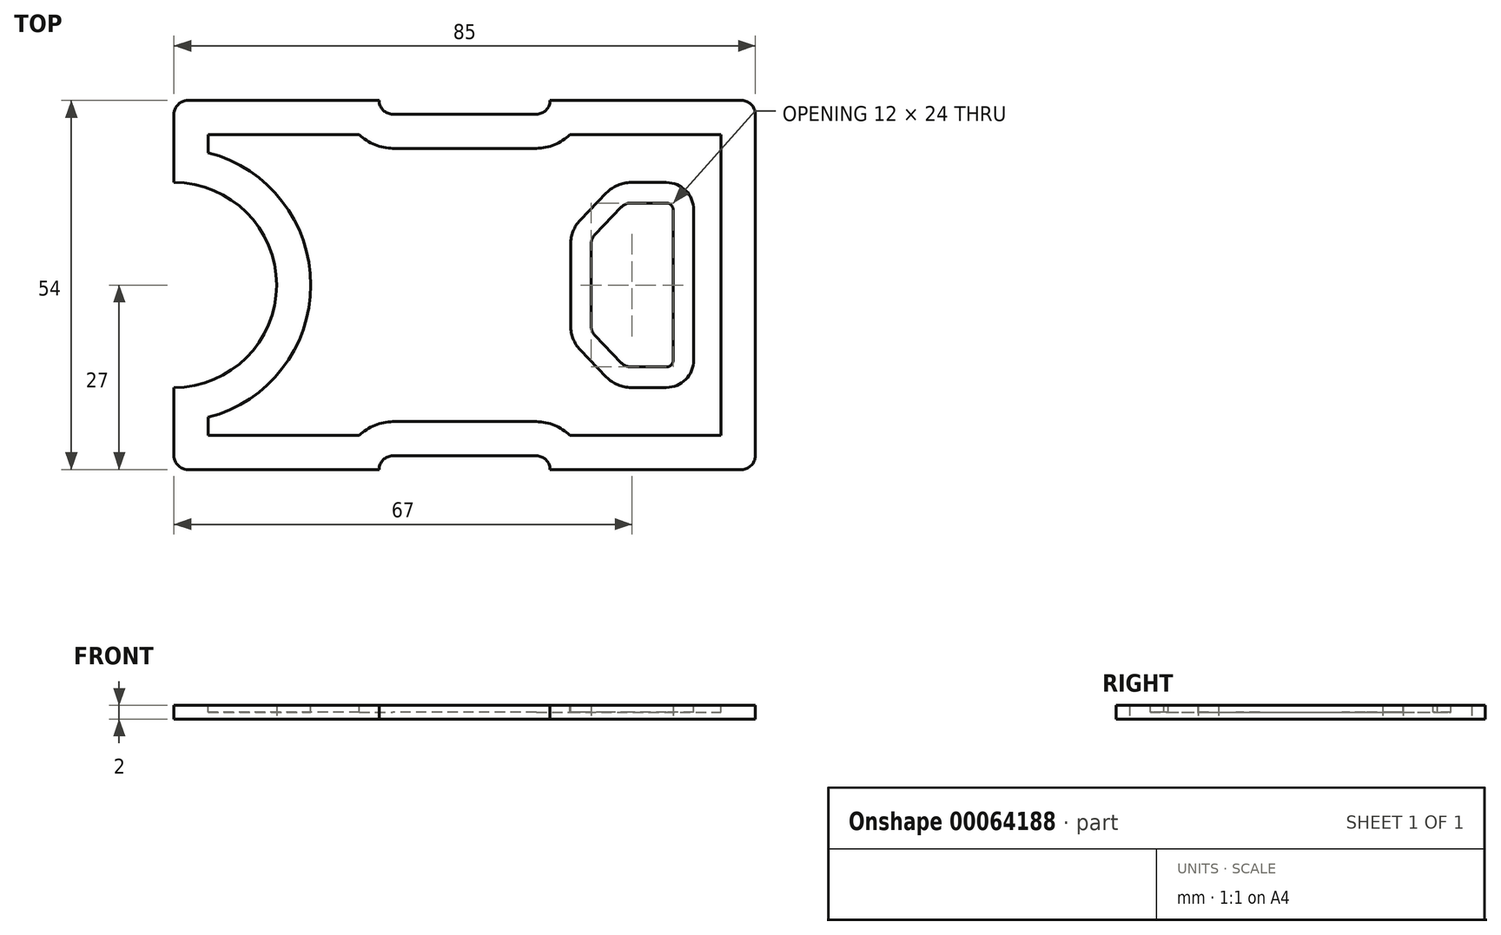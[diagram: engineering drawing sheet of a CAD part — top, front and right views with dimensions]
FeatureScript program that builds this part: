
annotation { "Feature Type Name" : "Feature", "Feature Type Description" : "" }
export const myFeature = defineFeature(function(context is Context, id is Id, definition is map)
    precondition{}
    {
        {
            var Q0;
            Q0=qCreatedBy(makeId("Top.planeOp"),FACE);
            var sketch = newSketch(context, id + "F0", { "sketchPlane" : qUnion([Q0])});
            skLineSegment(sketch, "E0.rect.bottom", {"start": v(40.5, -27) * mm, "end": v(-40.5, -27) * mm});
            skLineSegment(sketch, "E0.rect.top", {"start": v(40.5, 27) * mm, "end": v(-40.5, 27) * mm});
            skLineSegment(sketch, "E0.rect.left", {"start": v(42.5, -25) * mm, "end": v(42.5, 25) * mm});
            skLineSegment(sketch, "E0.rect.right", {"start": v(-42.5, -25) * mm, "end": v(-42.5, 25) * mm});
            skPoint(sketch, "E0.rect.middle", {"position": v(0, 0) * mm});
            skPoint(sketch, "E1.visualSharp", {"position": v(-42.5, 27) * mm});
            skArc(sketch, "E1.filletArc", {"start": v(-40.5, 27) * mm, "mid": v(-41.91, 26.41) * mm, "end": v(-42.5, 25) * mm});
            skPoint(sketch, "E2.visualSharp", {"position": v(-42.5, -27) * mm});
            skArc(sketch, "E2.filletArc", {"start": v(-42.5, -25) * mm, "mid": v(-41.91, -26.41) * mm, "end": v(-40.5, -27) * mm});
            skPoint(sketch, "E3.visualSharp", {"position": v(42.5, -27) * mm});
            skArc(sketch, "E3.filletArc", {"start": v(40.5, -27) * mm, "mid": v(41.91, -26.41) * mm, "end": v(42.5, -25) * mm});
            skPoint(sketch, "E4.visualSharp", {"position": v(42.5, 27) * mm});
            skArc(sketch, "E4.filletArc", {"start": v(42.5, 25) * mm, "mid": v(41.91, 26.41) * mm, "end": v(40.5, 27) * mm});
            skArc(sketch, "E5", {"start": v(-42.5, -15) * mm, "mid": v(-27.5, 0) * mm, "end": v(-42.5, 15) * mm});
            skLineSegment(sketch, "E6", {"start": v(30.5, 0) * mm, "end": v(30.5, -11) * mm});
            skLineSegment(sketch, "E7", {"start": v(29.5, -12) * mm, "end": v(24.35, -12) * mm});
            skLineSegment(sketch, "E8", {"start": v(22.9, -11.39) * mm, "end": v(19.06, -7.39) * mm});
            skLineSegment(sketch, "E9", {"start": v(18.5, -6) * mm, "end": v(18.5, 0) * mm});
            skLineSegment(sketch, "E10.MirrorCS", {"start": v(30.5, 0) * mm, "end": v(30.5, 11) * mm});
            skLineSegment(sketch, "E11.MirrorCS", {"start": v(29.5, 12) * mm, "end": v(24.35, 12) * mm});
            skLineSegment(sketch, "E12.MirrorCS", {"start": v(22.9, 11.39) * mm, "end": v(19.06, 7.39) * mm});
            skLineSegment(sketch, "E13.MirrorCS", {"start": v(18.5, 6) * mm, "end": v(18.5, 0) * mm});
            skPoint(sketch, "E14.visualSharp", {"position": v(18.5, -6.8) * mm});
            skArc(sketch, "E14.filletArc", {"start": v(18.5, -6) * mm, "mid": v(18.65, -6.75) * mm, "end": v(19.06, -7.39) * mm});
            skPoint(sketch, "E15.visualSharp", {"position": v(23.5, -12) * mm});
            skArc(sketch, "E15.filletArc", {"start": v(22.9, -11.39) * mm, "mid": v(23.57, -11.84) * mm, "end": v(24.35, -12) * mm});
            skPoint(sketch, "E16.visualSharp", {"position": v(30.5, -12) * mm});
            skArc(sketch, "E16.filletArc", {"start": v(29.5, -12) * mm, "mid": v(30.2, -11.7) * mm, "end": v(30.5, -11) * mm});
            skPoint(sketch, "E17.visualSharp", {"position": v(30.5, 12) * mm});
            skArc(sketch, "E17.filletArc", {"start": v(30.5, 11) * mm, "mid": v(30.2, 11.7) * mm, "end": v(29.5, 12) * mm});
            skPoint(sketch, "E18.visualSharp", {"position": v(23.5, 12) * mm});
            skArc(sketch, "E18.filletArc", {"start": v(24.35, 12) * mm, "mid": v(23.57, 11.84) * mm, "end": v(22.9, 11.39) * mm});
            skPoint(sketch, "E19.visualSharp", {"position": v(18.5, 6.8) * mm});
            skArc(sketch, "E19.filletArc", {"start": v(19.06, 7.39) * mm, "mid": v(18.65, 6.75) * mm, "end": v(18.5, 6) * mm});
            skLineSegment(sketch, "E20.rect.bottom", {"start": v(10.5, 25) * mm, "end": v(-10.5, 25) * mm});
            skPoint(sketch, "E20.rect.middle", {"position": v(0, 27) * mm});
            skLineSegment(sketch, "E21.rect.top", {"start": v(10.5, -25) * mm, "end": v(-10.5, -25) * mm});
            skPoint(sketch, "E21.rect.middle", {"position": v(0, -27) * mm});
            skPoint(sketch, "E22.orphan", {"position": v(-10.5, 29) * mm});
            skPoint(sketch, "E23.orphan", {"position": v(10.5, 29) * mm});
            skPoint(sketch, "E24.orphan", {"position": v(-10.5, -29) * mm});
            skPoint(sketch, "E25.orphan", {"position": v(10.5, -29) * mm});
            skArc(sketch, "E26", {"start": v(-12.5, 27) * mm, "mid": v(-11.91, 25.59) * mm, "end": v(-10.5, 25) * mm});
            skArc(sketch, "E27", {"start": v(10.5, 25) * mm, "mid": v(11.91, 25.59) * mm, "end": v(12.5, 27) * mm});
            skArc(sketch, "E28", {"start": v(-10.5, -25) * mm, "mid": v(-11.91, -25.59) * mm, "end": v(-12.5, -27) * mm});
            skArc(sketch, "E29", {"start": v(12.5, -27) * mm, "mid": v(11.91, -25.59) * mm, "end": v(10.5, -25) * mm});
            skSolve(sketch);
        }
        {
            var Q0;
            Q0=makeQuery(id+"F0.imprint","IMPRINT",FACE,{"disambiguationData":[TD([[makeQuery(id+"F0.imprint","IMPRINT",EDGE,{"derivedFrom":sQuery(id+"F0.wireOp",EDGE,"E0.rect.left")}),1.0]])]});
            extrude(context, id + "F1", {"entities" : qUnion([Q0]), "depth" : 2 * mm});
        }
        {
            var Q0;
            Q0=makeQuery(id+"F1.opExtrude","CAP_FACE",FACE,{"disambiguationData":[OSD([sQuery(id+"F0.wireOp",EDGE,"E0.rect.bottom"),sQuery(id+"F0.wireOp",EDGE,"E0.rect.top"),sQuery(id+"F0.wireOp",EDGE,"E0.rect.left"),sQuery(id+"F0.wireOp",EDGE,"E0.rect.right"),sQuery(id+"F0.wireOp",EDGE,"E1.filletArc"),sQuery(id+"F0.wireOp",EDGE,"E2.filletArc"),sQuery(id+"F0.wireOp",EDGE,"E3.filletArc"),sQuery(id+"F0.wireOp",EDGE,"E4.filletArc"),sQuery(id+"F0.wireOp",EDGE,"E5"),sQuery(id+"F0.wireOp",EDGE,"E6"),sQuery(id+"F0.wireOp",EDGE,"E7"),sQuery(id+"F0.wireOp",EDGE,"E8"),sQuery(id+"F0.wireOp",EDGE,"E9"),sQuery(id+"F0.wireOp",EDGE,"E10.MirrorCS"),sQuery(id+"F0.wireOp",EDGE,"E11.MirrorCS"),sQuery(id+"F0.wireOp",EDGE,"E12.MirrorCS"),sQuery(id+"F0.wireOp",EDGE,"E13.MirrorCS"),sQuery(id+"F0.wireOp",EDGE,"E14.filletArc"),sQuery(id+"F0.wireOp",EDGE,"E15.filletArc"),sQuery(id+"F0.wireOp",EDGE,"E16.filletArc"),sQuery(id+"F0.wireOp",EDGE,"E17.filletArc"),sQuery(id+"F0.wireOp",EDGE,"E18.filletArc"),sQuery(id+"F0.wireOp",EDGE,"E19.filletArc"),sQuery(id+"F0.wireOp",EDGE,"E20.rect.bottom"),sQuery(id+"F0.wireOp",EDGE,"E21.rect.top"),sQuery(id+"F0.wireOp",EDGE,"E26"),sQuery(id+"F0.wireOp",EDGE,"E27"),sQuery(id+"F0.wireOp",EDGE,"E28"),sQuery(id+"F0.wireOp",EDGE,"E29")])],"isStart":false});
            var sketch = newSketch(context, id + "F2", { "sketchPlane" : qUnion([Q0])});
            skLineSegment(sketch, "E30.0", {"start": v(-12.5, 27) * mm, "end": v(-40.5, 27) * mm});
            skArc(sketch, "E31.0", {"start": v(-40.5, 27) * mm, "mid": v(-41.91, 26.41) * mm, "end": v(-42.5, 25) * mm});
            skLineSegment(sketch, "E32.0", {"start": v(-42.5, 15) * mm, "end": v(-42.5, 25) * mm});
            skArc(sketch, "E33.0", {"start": v(-42.5, -15) * mm, "mid": v(-27.5, 0) * mm, "end": v(-42.5, 15) * mm});
            skLineSegment(sketch, "E34.0", {"start": v(-42.5, -25) * mm, "end": v(-42.5, -15) * mm});
            skArc(sketch, "E35.0", {"start": v(-42.5, -25) * mm, "mid": v(-41.91, -26.41) * mm, "end": v(-40.5, -27) * mm});
            skLineSegment(sketch, "E36.0", {"start": v(-12.5, -27) * mm, "end": v(-40.5, -27) * mm});
            skLineSegment(sketch, "E37.0", {"start": v(40.5, -27) * mm, "end": v(12.5, -27) * mm});
            skArc(sketch, "E38.0", {"start": v(40.5, -27) * mm, "mid": v(41.91, -26.41) * mm, "end": v(42.5, -25) * mm});
            skLineSegment(sketch, "E39.0", {"start": v(42.5, -25) * mm, "end": v(42.5, 25) * mm});
            skArc(sketch, "E40.0", {"start": v(42.5, 25) * mm, "mid": v(41.91, 26.41) * mm, "end": v(40.5, 27) * mm});
            skLineSegment(sketch, "E41.0", {"start": v(40.5, 27) * mm, "end": v(12.5, 27) * mm});
            skArc(sketch, "E42.0", {"start": v(-12.5, 27) * mm, "mid": v(-11.91, 25.59) * mm, "end": v(-10.5, 25) * mm});
            skLineSegment(sketch, "E43.0", {"start": v(10.5, 25) * mm, "end": v(-10.5, 25) * mm});
            skArc(sketch, "E44.0", {"start": v(10.5, 25) * mm, "mid": v(11.91, 25.59) * mm, "end": v(12.5, 27) * mm});
            skArc(sketch, "E45.0", {"start": v(12.5, -27) * mm, "mid": v(11.91, -25.59) * mm, "end": v(10.5, -25) * mm});
            skLineSegment(sketch, "E46.0", {"start": v(10.5, -25) * mm, "end": v(-10.5, -25) * mm});
            skArc(sketch, "E47.0", {"start": v(-10.5, -25) * mm, "mid": v(-11.91, -25.59) * mm, "end": v(-12.5, -27) * mm});
            skLineSegment(sketch, "E48.0", {"start": v(22.9, 11.39) * mm, "end": v(19.06, 7.39) * mm});
            skArc(sketch, "E49.0", {"start": v(19.06, 7.39) * mm, "mid": v(18.65, 6.75) * mm, "end": v(18.5, 6) * mm});
            skLineSegment(sketch, "E50.0", {"start": v(18.5, -6) * mm, "end": v(18.5, 6) * mm});
            skArc(sketch, "E51.0", {"start": v(18.5, -6) * mm, "mid": v(18.65, -6.75) * mm, "end": v(19.06, -7.39) * mm});
            skLineSegment(sketch, "E52.0", {"start": v(22.9, -11.39) * mm, "end": v(19.06, -7.39) * mm});
            skArc(sketch, "E53.0", {"start": v(22.9, -11.39) * mm, "mid": v(23.57, -11.84) * mm, "end": v(24.35, -12) * mm});
            skLineSegment(sketch, "E54.0", {"start": v(29.5, -12) * mm, "end": v(24.35, -12) * mm});
            skArc(sketch, "E55.0", {"start": v(29.5, -12) * mm, "mid": v(30.2, -11.7) * mm, "end": v(30.5, -11) * mm});
            skLineSegment(sketch, "E56.0", {"start": v(30.5, -11) * mm, "end": v(30.5, 11) * mm});
            skArc(sketch, "E57.0", {"start": v(30.5, 11) * mm, "mid": v(30.2, 11.7) * mm, "end": v(29.5, 12) * mm});
            skLineSegment(sketch, "E58.0", {"start": v(29.5, 12) * mm, "end": v(24.35, 12) * mm});
            skArc(sketch, "E59.0", {"start": v(-14.5, 24) * mm, "mid": v(-12.74, 22.53) * mm, "end": v(-10.5, 22) * mm});
            skLineSegment(sketch, "E59.1", {"start": v(10.5, 22) * mm, "end": v(-10.5, 22) * mm});
            skArc(sketch, "E59.2", {"start": v(10.5, 22) * mm, "mid": v(12.74, 22.53) * mm, "end": v(14.5, 24) * mm});
            skLineSegment(sketch, "E59.3", {"start": v(-14.5, -24) * mm, "end": v(-39.5, -24) * mm});
            skLineSegment(sketch, "E59.4", {"start": v(-39.5, -24) * mm, "end": v(-39.5, -17.75) * mm});
            skArc(sketch, "E59.5", {"start": v(-39.5, -17.75) * mm, "mid": v(-24.5, 0) * mm, "end": v(-39.5, 17.75) * mm});
            skLineSegment(sketch, "E59.6", {"start": v(-39.5, 17.75) * mm, "end": v(-39.5, 24) * mm});
            skArc(sketch, "E59.7", {"start": v(-10.5, -22) * mm, "mid": v(-12.74, -22.53) * mm, "end": v(-14.5, -24) * mm});
            skLineSegment(sketch, "E59.8", {"start": v(10.5, -22) * mm, "end": v(-10.5, -22) * mm});
            skArc(sketch, "E59.9", {"start": v(14.5, -24) * mm, "mid": v(12.74, -22.53) * mm, "end": v(10.5, -22) * mm});
            skLineSegment(sketch, "E59.10", {"start": v(-14.5, 24) * mm, "end": v(-39.5, 24) * mm});
            skLineSegment(sketch, "E59.11", {"start": v(39.5, -24) * mm, "end": v(14.5, -24) * mm});
            skLineSegment(sketch, "E59.12", {"start": v(39.5, -24) * mm, "end": v(39.5, 24) * mm});
            skLineSegment(sketch, "E59.13", {"start": v(39.5, 24) * mm, "end": v(14.5, 24) * mm});
            skArc(sketch, "E60.0", {"start": v(33.5, 11) * mm, "mid": v(32.33, 13.83) * mm, "end": v(29.5, 15) * mm});
            skLineSegment(sketch, "E60.1", {"start": v(15.5, -6) * mm, "end": v(15.5, 6) * mm});
            skArc(sketch, "E60.2", {"start": v(16.9, 9.47) * mm, "mid": v(15.86, 7.87) * mm, "end": v(15.5, 6) * mm});
            skLineSegment(sketch, "E60.3", {"start": v(20.75, 13.47) * mm, "end": v(16.9, 9.47) * mm});
            skArc(sketch, "E60.4", {"start": v(24.35, 15) * mm, "mid": v(22.4, 14.6) * mm, "end": v(20.75, 13.47) * mm});
            skArc(sketch, "E60.5", {"start": v(15.5, -6) * mm, "mid": v(15.86, -7.87) * mm, "end": v(16.9, -9.47) * mm});
            skLineSegment(sketch, "E60.6", {"start": v(29.5, 15) * mm, "end": v(24.35, 15) * mm});
            skLineSegment(sketch, "E60.7", {"start": v(20.75, -13.47) * mm, "end": v(16.9, -9.47) * mm});
            skArc(sketch, "E60.8", {"start": v(20.75, -13.47) * mm, "mid": v(22.4, -14.6) * mm, "end": v(24.35, -15) * mm});
            skLineSegment(sketch, "E60.9", {"start": v(29.5, -15) * mm, "end": v(24.35, -15) * mm});
            skArc(sketch, "E60.10", {"start": v(29.5, -15) * mm, "mid": v(32.33, -13.83) * mm, "end": v(33.5, -11) * mm});
            skLineSegment(sketch, "E60.11", {"start": v(33.5, -11) * mm, "end": v(33.5, 11) * mm});
            skArc(sketch, "E61.0", {"start": v(10.5, -20) * mm, "mid": v(13.15, -20.52) * mm, "end": v(15.4, -22) * mm});
            skLineSegment(sketch, "E61.1", {"start": v(-10.5, -20) * mm, "end": v(10.5, -20) * mm});
            skArc(sketch, "E61.2", {"start": v(-15.4, -22) * mm, "mid": v(-13.15, -20.52) * mm, "end": v(-10.5, -20) * mm});
            skLineSegment(sketch, "E61.3", {"start": v(10.5, 20) * mm, "end": v(-10.5, 20) * mm});
            skArc(sketch, "E61.4", {"start": v(15.4, 22) * mm, "mid": v(13.15, 20.52) * mm, "end": v(10.5, 20) * mm});
            skLineSegment(sketch, "E61.5", {"start": v(37.5, 22) * mm, "end": v(15.4, 22) * mm});
            skLineSegment(sketch, "E61.6", {"start": v(37.5, -22) * mm, "end": v(37.5, 22) * mm});
            skArc(sketch, "E61.7", {"start": v(-10.5, 20) * mm, "mid": v(-13.15, 20.52) * mm, "end": v(-15.4, 22) * mm});
            skLineSegment(sketch, "E61.8", {"start": v(-15.4, 22) * mm, "end": v(-37.5, 22) * mm});
            skLineSegment(sketch, "E61.9", {"start": v(-37.5, 22) * mm, "end": v(-37.5, 19.36) * mm});
            skLineSegment(sketch, "E61.10", {"start": v(15.4, -22) * mm, "end": v(37.5, -22) * mm});
            skArc(sketch, "E61.11", {"start": v(-37.5, 19.36) * mm, "mid": v(-22.5, 0) * mm, "end": v(-37.5, -19.36) * mm});
            skLineSegment(sketch, "E61.12", {"start": v(-37.5, -19.36) * mm, "end": v(-37.5, -22) * mm});
            skLineSegment(sketch, "E61.13", {"start": v(-37.5, -22) * mm, "end": v(-15.4, -22) * mm});
            skSolve(sketch);
        }
        {
            var Q0;
            Q0=makeQuery(id+"F2.imprint","IMPRINT",FACE,{"disambiguationData":[TD([[makeQuery(id+"F2.imprint","IMPRINT",EDGE,{"derivedFrom":sQuery(id+"F2.wireOp",EDGE,"E60.0")}),-1.0]])]});
            extrude(context, id + "F3", {"entities" : qUnion([Q0]), "operationType" : NewBodyOperationType.REMOVE, "oppositeDirection" : true, "depth" : 1 * mm});
        }
    });
